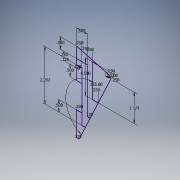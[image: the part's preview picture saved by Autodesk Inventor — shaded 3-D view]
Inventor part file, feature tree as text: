
AUTODESK INVENTOR PART (.ipt)
format: ipt  version: 2017 (Build 210142000, 142)  size: 111,616 bytes
history: native  units: in
note: dims shown in document units (in); Inventor stores cm internally (conversion verified against a paired STEP export)
features: sketch x1
ambient origin geometry x8: Origin, YZ Plane, XZ Plane, XY Plane, X Axis, Y Axis, Z Axis, Center Point
feature tree (1):
  sketch  "Sketch1"  dims[d0=0.25in d1=0.1718in d2=15.0deg d4=0.25in d5=1.5in d6=1.25in d7=0.25in d11=0.25in d13=0.5in d15=0.25in d16=0.25in d18=0.125in d19=0.5in d20=0.125in d21=0.25in d22=0.125in d23=0.125in d24=0.25in d25=0.5in d26=2.292in d27=0.5in]
